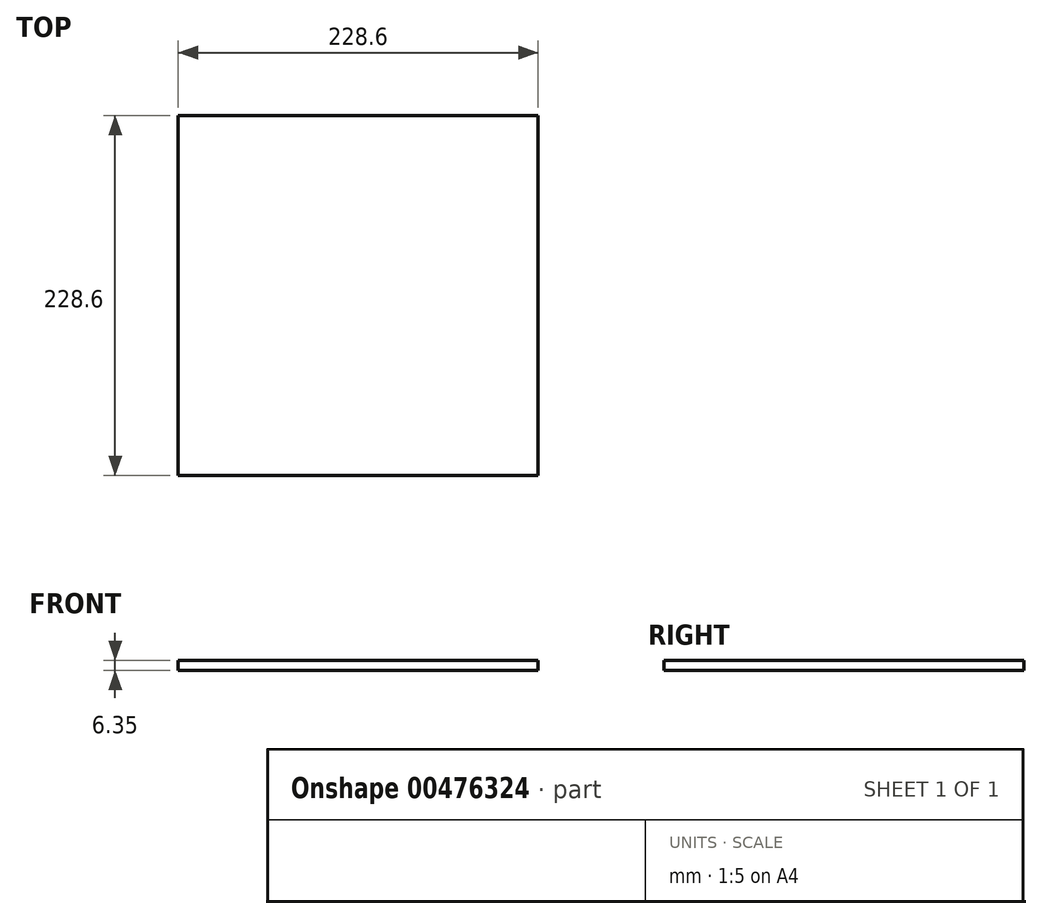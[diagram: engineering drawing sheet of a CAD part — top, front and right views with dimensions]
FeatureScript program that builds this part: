
annotation { "Feature Type Name" : "Feature", "Feature Type Description" : "" }
export const myFeature = defineFeature(function(context is Context, id is Id, definition is map)
    precondition{}
    {
        {
            var Q0;
            Q0=qCreatedBy(makeId("Top.planeOp"),FACE);
            var sketch = newSketch(context, id + "F0", { "sketchPlane" : qUnion([Q0])});
            skLineSegment(sketch, "E0.bottom", {"start": v(0, 0) * mm, "end": v(228.6, 0) * mm});
            skLineSegment(sketch, "E0.top", {"start": v(0, -228.6) * mm, "end": v(228.6, -228.6) * mm});
            skLineSegment(sketch, "E0.left", {"start": v(0, 0) * mm, "end": v(0, -228.6) * mm});
            skLineSegment(sketch, "E0.right", {"start": v(228.6, 0) * mm, "end": v(228.6, -228.6) * mm});
            skSolve(sketch);
        }
        {
            var Q0;
            Q0 = qSketchRegion(id + "F0", true);
            extrude(context, id + "F1", {"entities" : qUnion([Q0]), "depth" : 6.35 * mm});
        }
    });
